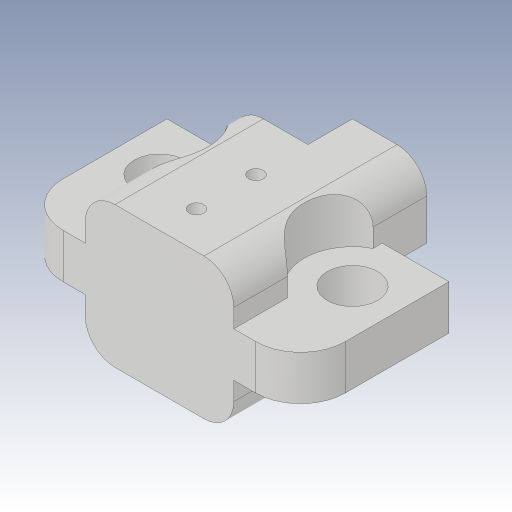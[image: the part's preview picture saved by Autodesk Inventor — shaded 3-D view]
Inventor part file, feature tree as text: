
AUTODESK INVENTOR PART (.ipt)
format: ipt  version: 2023.3 (Build 273359000, 359)  size: 302,080 bytes
history: native  units: in
note: dims shown in document units (in); Inventor stores cm internally (conversion verified against a paired STEP export)
features: sketch x8, hole x6, projected_geometry x6, extrude x3, fillet x1
ambient origin geometry x8: Origin, YZ Plane, XZ Plane, XY Plane, X Axis, Y Axis, Z Axis, Center Point
bodies: Body1 (feature_tree)
feature tree (24):
  sketch  "Skizze3"  dims[d9=0.3937in d10=0.0in d12=0.3937in]
  extrude  "Extrusion3"  Depth=0.3937in
  extrude  "Extrusion4"  Depth=0.3937in
  fillet  "Rundung1"  Radius=0.3937in
  sketch  "Skizze5"  dims[d13=0.374in d14=0.0787in d17=0.3937in d18=0.0in]
  hole  "Bohrung3"  [1 undecoded]
  sketch  "Skizze6"  dims[d19=0.1181in]
  hole  "Bohrung5"  [1 undecoded]
  sketch  "Skizze9"  dims[d42=0.1181in d43=0.0in]
  hole  "Bohrung6"  [1 undecoded]
  hole  "Bohrung7"  [1 undecoded]
  hole  "Bohrung8"  [1 undecoded]
  extrude  "Extrusion7"  Depth=0.0197in
  hole  "Bohrung9"  [1 undecoded]
  sketch  "Skizze7"  dims[d34=0.2362in d35=0.2362in d36=0.4331in d37=0.0984in d38=90.0deg d39=0.4724in d40=0.0in d41=0.1181in]
  projected_geometry  "Projizierte Kontur2"
  projected_geometry  "Projizierte Kontur3"
  sketch  "Skizze10"  dims[d52=0.0394in d53=0.2362in d54=0.1575in d55=0.0787in d56=90.0deg d57=0.315in d58=0.0in d83=0.1772in]
  sketch  "Skizze11"  dims[d84=0.1181in]
  projected_geometry  "Projizierte Kontur4"
  projected_geometry  "Projizierte Kontur5"
  projected_geometry  "Projizierte Kontur6"
  sketch  "Skizze12"  dims[d85=0.1339in d86=0.2362in d87=0.2559in d88=0.1339in d89=0.5635in d90=0.4724in d91=0.0in d92=0.1339in d93=0.2362in d94=0.2559in d95=0.1339in d96=90.0deg d97=0.315in d98=0.0in d99=0.1339in d100=0.2362in d101=0.2559in d102=0.1339in d103=90.0deg d104=0.315in d105=0.0in d106=0.1181in d107=0.0in d108=0.1181in d109=0.0in d113=0.0591in d114=0.0394in d115=0.2362in d116=0.1575in d117=0.0787in d118=90.0deg d119=0.315in d120=0.0in d122=0.2165in d8=0.0197in d11=0.0344in d79=0.0in d80=0.0in d81=0.0in d82=0.0in]
  projected_geometry  "Projizierte Kontur7"
note: 6 required parameter values undecoded (feature->parameter linkage not recoverable at this tier; creation-order binding heuristic only, values carry confidence <= 0.55)
